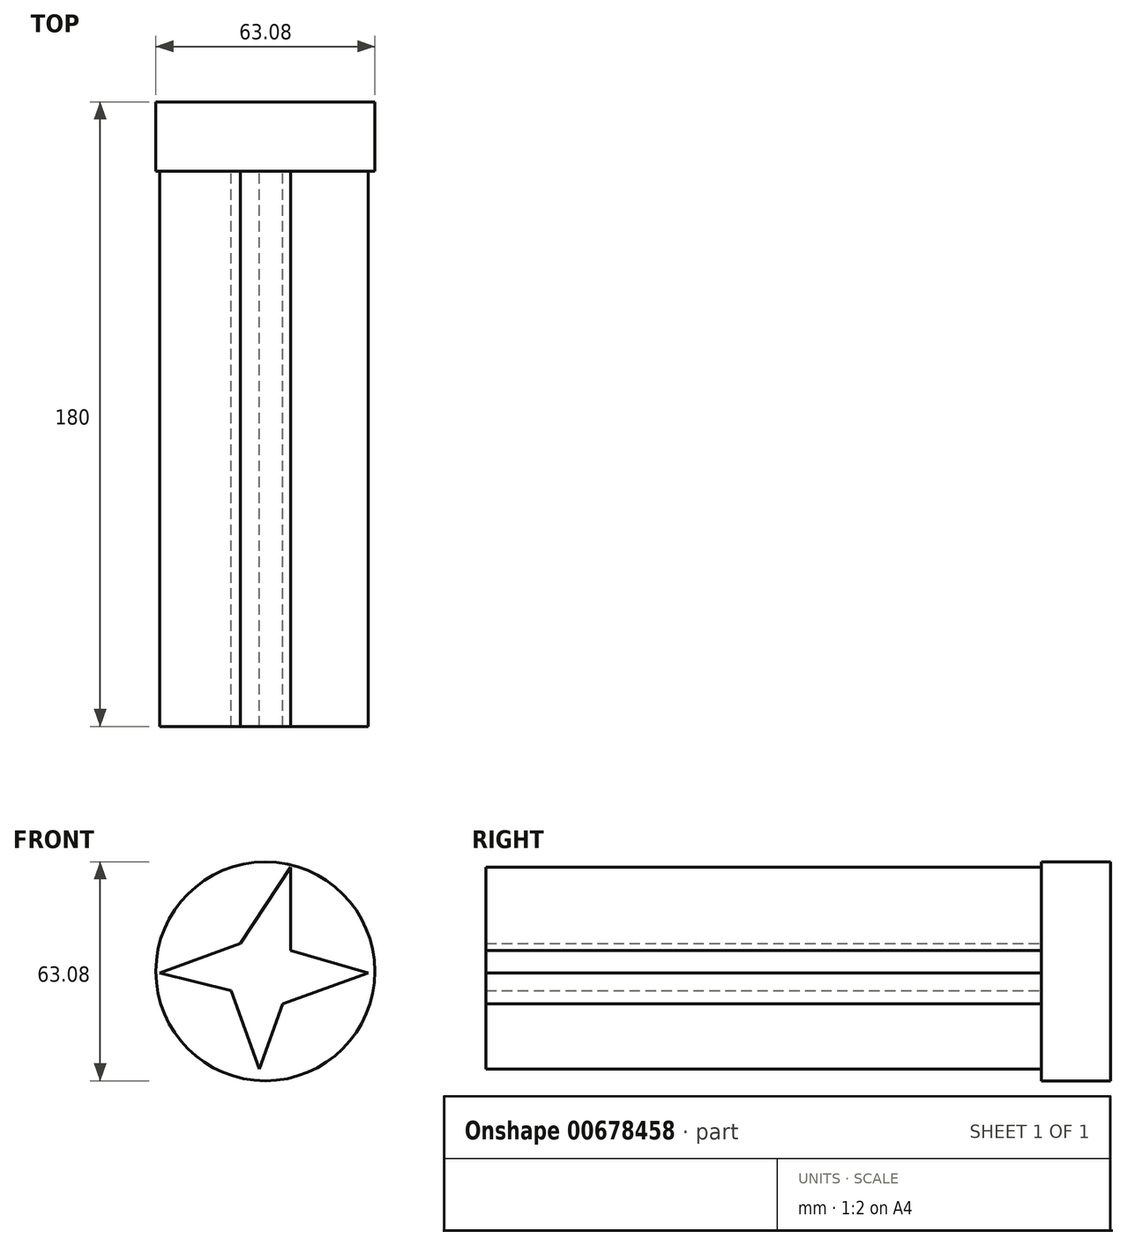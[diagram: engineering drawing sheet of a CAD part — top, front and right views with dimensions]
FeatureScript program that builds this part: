
annotation { "Feature Type Name" : "Feature", "Feature Type Description" : "" }
export const myFeature = defineFeature(function(context is Context, id is Id, definition is map)
    precondition{}
    {
        {
            var Q0;
            Q0=qCreatedBy(makeId("Front.planeOp"),FACE);
            var sketch = newSketch(context, id + "F0", { "sketchPlane" : qUnion([Q0])});
            skLineSegment(sketch, "E0", {"start": v(7.28, 29.95) * mm, "end": v(7.28, 6) * mm});
            skLineSegment(sketch, "E1", {"start": v(7.28, 6) * mm, "end": v(29.65, -0.42) * mm});
            skLineSegment(sketch, "E2", {"start": v(29.65, -0.42) * mm, "end": v(4.97, -9.35) * mm});
            skLineSegment(sketch, "E3", {"start": v(4.97, -9.35) * mm, "end": v(-1.75, -28.15) * mm});
            skLineSegment(sketch, "E4", {"start": v(-1.75, -28.15) * mm, "end": v(-9.9, -5.6) * mm});
            skLineSegment(sketch, "E5", {"start": v(-9.9, -5.6) * mm, "end": v(-30.4, -0.42) * mm});
            skLineSegment(sketch, "E6", {"start": v(-30.4, -0.42) * mm, "end": v(-7.14, 7.99) * mm});
            skLineSegment(sketch, "E7", {"start": v(-7.14, 7.99) * mm, "end": v(7.28, 29.95) * mm});
            skSolve(sketch);
        }
        {
            var Q0;
            Q0=makeQuery(id+"F0.imprint","IMPRINT",FACE,{"disambiguationData":[TD([[makeQuery(id+"F0.imprint","IMPRINT",EDGE,{"derivedFrom":sQuery(id+"F0.wireOp",EDGE,"E0")}),-1.0]])]});
            var Q1;
            Q1=sQuery(id+"F0.wireOp",EDGE,"E0");
            var Q2;
            Q2=sQuery(id+"F0.wireOp",EDGE,"E1");
            var Q3;
            Q3=sQuery(id+"F0.wireOp",EDGE,"E2");
            var Q4;
            Q4=sQuery(id+"F0.wireOp",EDGE,"E3");
            var Q5;
            Q5=sQuery(id+"F0.wireOp",EDGE,"E4");
            var Q6;
            Q6=sQuery(id+"F0.wireOp",EDGE,"E5");
            var Q7;
            Q7=sQuery(id+"F0.wireOp",EDGE,"E6");
            var Q8;
            Q8=sQuery(id+"F0.wireOp",EDGE,"E7");
            extrude(context, id + "F1", {"entities" : qUnion([Q0]), "surfaceEntities" : qUnion([Q1, Q2, Q3, Q4, Q5, Q6, Q7, Q8]), "depth" : 180 * mm, "offsetDistance" : 25 * mm});
        }
        {
            var Q0;
            Q0=makeQuery(id+"F0.imprint","IMPRINT",FACE,{"disambiguationData":[TD([[makeQuery(id+"F0.imprint","IMPRINT",EDGE,{"derivedFrom":sQuery(id+"F0.wireOp",EDGE,"E0")}),-1.0]])]});
            var sketch = newSketch(context, id + "F2", { "sketchPlane" : qUnion([Q0])});
            skCircle(sketch, "E8", {"center": v(0, 0) * mm, "radius": 31.54 * mm});
            skSolve(sketch);
        }
        {
            var Q0;
            Q0 = qSketchRegion(id + "F2", true);
            extrude(context, id + "F3", {"entities" : qUnion([Q0]), "operationType" : NewBodyOperationType.ADD, "depth" : 20 * mm, "offsetDistance" : 25 * mm});
        }
    });
